# Revit family: BLAUBERG-KOMFORT_EC_DBE_550_Right
name_source: partatom
category: Mechanical Equipment
units: mm (PartAtom-declared; Revit-internal decimal feet)

## family parameters
Always vertical = Yes
Classification = None
Cut with Voids When Loaded = No
OmniClass Number = 23.75.35.14
OmniClass Title = Air Handling Units
Part Type = Normal
Room Calculation Point = No
Round Connector Dimension = Use Diameter
Shared = No
Work Plane-Based = No

## types (2) — shared parameters
B = 828 mm  [stored 2.71654 ft]
B1 = 295 mm  [stored 0.967848 ft]
B2 = 188 mm  [stored 0.616798 ft]
Casing Material = Painted Steel Gray
Current = 11 A
D = 200 mm  [stored 0.656168 ft]
DPS_H = 170 mm  [stored 0.557743 ft]
DPS_L1 = 145 mm  [stored 0.475722 ft]
DPS_L2 = 410 mm  [stored 1.34514 ft]
Description = Air Handling Unit
Duct Connection Diameter = 200 mm  [stored 0.656168 ft]
ElBoxB = 24 mm  [stored 0.0787402 ft]
ElBoxB1 = 22 mm  [stored 0.0721785 ft]
ElBoxL = 302 mm  [stored 0.990814 ft]
Extract Air Filter = G4
Family Version = 1.0
Front Maintenance Zone Height = 850 mm  [stored 2.78871 ft]
Front Maintenance Zone Length = 1238 mm  [stored 4.06168 ft]
Front Maintenance Zone Width = 280 mm  [stored 0.918635 ft]
H = 280 mm  [stored 0.918635 ft]
H1 = 118 mm
HDrainCon = 31 mm  [stored 0.101706 ft]
Heat Exchanger Type = counter-flow
Heater power = 2000 W
L = 1238 mm  [stored 4.06168 ft]
LDrainCon = 28 mm  [stored 0.0918635 ft]
LDrainCon1 = 280 mm  [stored 0.918635 ft]
LDrainCon2 = 437 mm  [stored 1.43373 ft]
LDuctCon = 50 mm  [stored 0.164042 ft]
Load Classification = HVAC
Maintenance Zone Material = Maintenance Zone
Manufacturer = Blauberg
Maximum Air Flow = 620 m³/h
Maximum Unit Current With Electric Heater = 11 A
Maximum Unit Current Without Electric Heater = 2 A
Maximum Unit Power Without Electric Heater = 297 W
Metal Material = Metal Zinc
Number of Poles = 1
Power = 2297 W
Power Factor = 1
RPM (min-1) = 3100
SEC Class = A
Sound Pressure Level at 3 m (dBA) = 30
Supply Air Filter = G4 (F7 option)
Transported Air Temperature (°C) = -25…+40
URL = https://blaubergventilatoren.de
Voltage = 230 V
Weight = 67.00 kg

## per-type parameters (varying)
| type | Drain Connection Diameter | DrainD | DrainPipe | Heat Exchanger Material | Heat recovery efficiency (%) | Type Comments |
| KOMFORT EC DBE 550 R S21 | 14 mm  [stored 0.0459318 ft] | 14 mm  [stored 0.0459318 ft] | Yes | polystyrene | 78..90 | Air Handling Unit KOMFORT EC DBE 550 R S21 |
| KOMFORT EC DBE 550-E R S21 | 0 mm  [stored 0 ft] | 1 mm  [stored 0.00328084 ft] | No | enthalpy | 69..87 | Air Handling Unit KOMFORT EC DBE 550-E R S21 |

note: column(s) folded — value = type name in every type: Model

note: [stored X ft] marks values corroborated as IEEE doubles in the binary element streams (Revit-internal decimal feet)

## geometry (parser evidence)
native form markers: Sweep x5
no freeform markers — native parametric forms only
